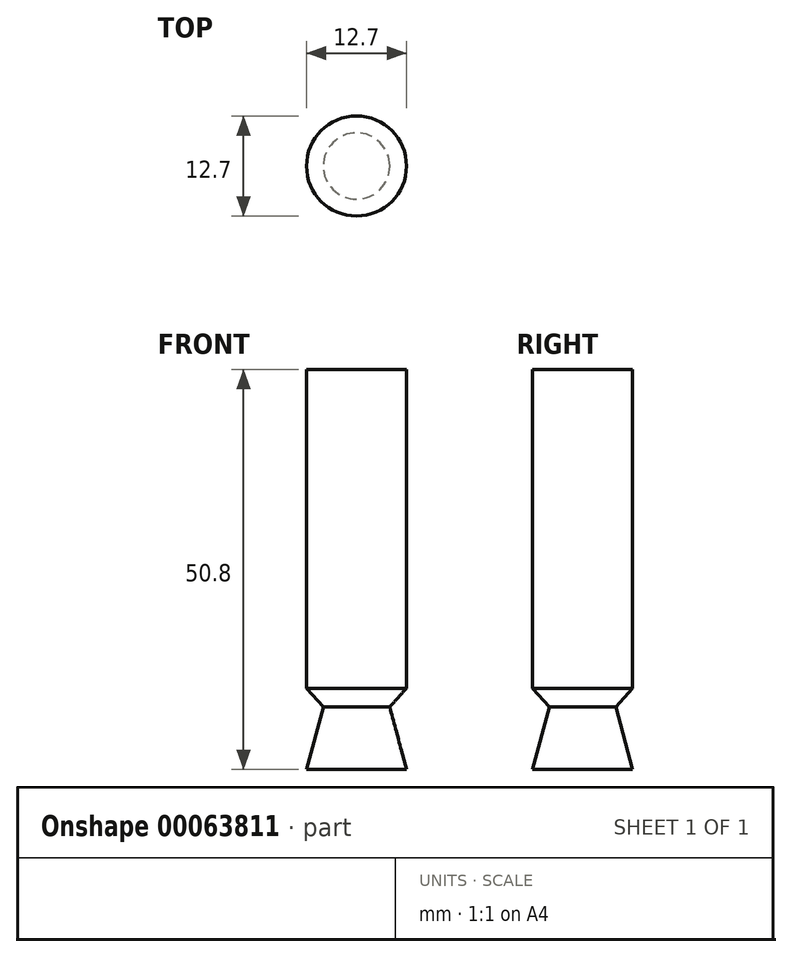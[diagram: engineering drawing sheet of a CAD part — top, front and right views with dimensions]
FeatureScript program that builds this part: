
annotation { "Feature Type Name" : "Feature", "Feature Type Description" : "" }
export const myFeature = defineFeature(function(context is Context, id is Id, definition is map)
    precondition{}
    {
        {
            var Q0;
            Q0=qCreatedBy(makeId("Front.planeOp"),FACE);
            var sketch = newSketch(context, id + "F0", { "sketchPlane" : qUnion([Q0])});
            skLineSegment(sketch, "E0", {"start": v(0, 0) * mm, "end": v(6.35, 0) * mm});
            skLineSegment(sketch, "E1", {"start": v(6.35, 0) * mm, "end": v(4.22, 7.94) * mm});
            skLineSegment(sketch, "E2", {"start": v(4.22, 7.94) * mm, "end": v(6.35, 10.32) * mm});
            skLineSegment(sketch, "E3", {"start": v(6.35, 10.32) * mm, "end": v(6.35, 50.8) * mm});
            skLineSegment(sketch, "E4", {"start": v(6.35, 50.8) * mm, "end": v(0, 50.8) * mm});
            skLineSegment(sketch, "E5", {"start": v(0, 50.8) * mm, "end": v(0, 0) * mm});
            skLineSegment(sketch, "E6", {"start": v(4.22, 7.94) * mm, "end": v(4.22, 15.3) * mm, "construction": true});
            skLineSegment(sketch, "E7.MirrorCS", {"start": v(-4.22, 7.94) * mm, "end": v(-4.22, 15.3) * mm, "construction": true});
            skLineSegment(sketch, "E8.MirrorCS", {"start": v(0, 0) * mm, "end": v(-6.35, 0) * mm, "construction": true});
            skLineSegment(sketch, "E9.MirrorCS", {"start": v(-6.35, 0) * mm, "end": v(-4.22, 7.94) * mm, "construction": true});
            skSolve(sketch);
        }
        {
            var Q0;
            Q0=makeQuery(id+"F0.imprint","IMPRINT",FACE,{"disambiguationData":[TD([[makeQuery(id+"F0.imprint","IMPRINT",EDGE,{"derivedFrom":sQuery(id+"F0.wireOp",EDGE,"E0")}),1.0]])]});
            var Q1;
            Q1=sQuery(id+"F0.wireOp",EDGE,"E5");
            revolve(context, id + "F1", {"surfaceOperationType" : NewSurfaceOperationType.NEW, "entities" : qUnion([Q0]), "axis" : qUnion([Q1]), "revolveType" : RevolveType.FULL});
        }
    });
